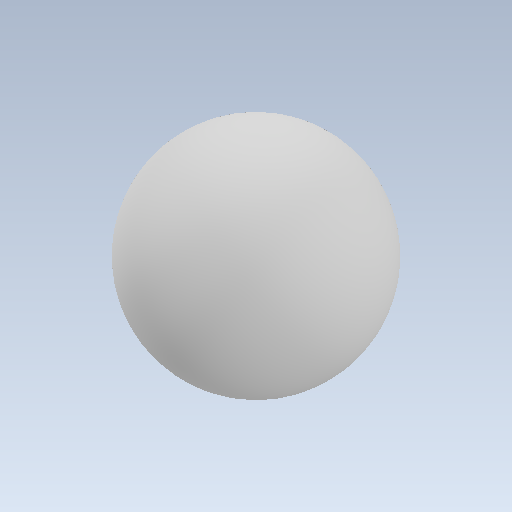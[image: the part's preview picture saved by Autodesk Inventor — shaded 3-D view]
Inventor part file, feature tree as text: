
AUTODESK INVENTOR PART (.ipt)
format: ipt  version: 2020 (Build 240168000, 168)  size: 116,224 bytes
history: native  units: mm
features: revolve x1, sketch x1
ambient origin geometry x8: Origin, YZ Plane, XZ Plane, XY Plane, X Axis, Y Axis, Z Axis, Center Point
bodies: Solid1 (feature_tree)
feature tree (2):
  revolve  "Revolution1"  Angle=90.0deg
  sketch  "Sketch1"  dims[d0=40.0mm d1=90.0deg]
